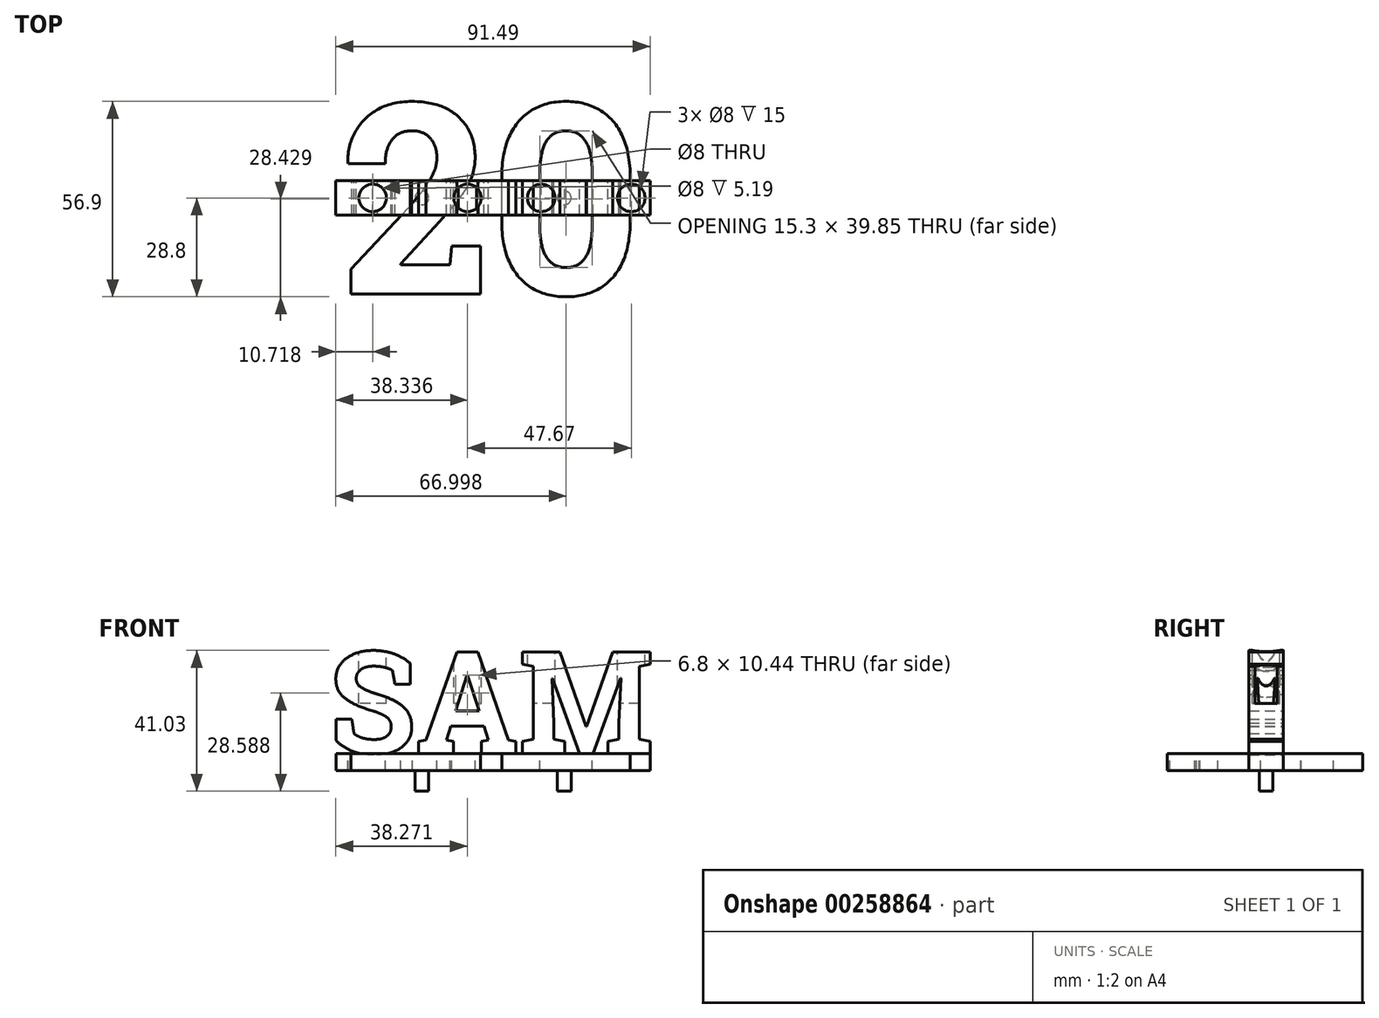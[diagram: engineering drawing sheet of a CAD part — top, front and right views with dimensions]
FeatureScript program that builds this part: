
annotation { "Feature Type Name" : "Feature", "Feature Type Description" : "" }
export const myFeature = defineFeature(function(context is Context, id is Id, definition is map)
    precondition{}
    {
        {
            var Q0;
            Q0=qCreatedBy(makeId("Front.planeOp"),FACE);
            var sketch = newSketch(context, id + "F0", { "sketchPlane" : qUnion([Q0])});
            skText(sketch, "E0", { "text": "SAM", "fontName": "RobotoSlab-Bold.ttf"});
            const initialGuessF0  = {"E0": [-0.048, 0, 1, 0, 0.03]};
            skSetInitialGuess(sketch, initialGuessF0);
            skSolve(sketch);
        }
        {
            var Q0;
            Q0 = qSketchRegion(id + "F0", true);
            extrude(context, id + "F1", {"entities" : qUnion([Q0]), "depth" : 10 * mm});
        }
        {
            var Q0;
            Q0=makeQuery(id+"F1.opExtrude","SWEPT_FACE",FACE,{"disambiguationData":[OSD([sQuery(id+"F0.wireOp",EDGE,"E0.sketch_text.stroke-44")])]});
            var sketch = newSketch(context, id + "F2", { "sketchPlane" : qUnion([Q0])});
            skLineSegment(sketch, "E1.bottom", {"start": v(45.46, 10) * mm, "end": v(-45.97, 10) * mm});
            skLineSegment(sketch, "E1.top", {"start": v(45.46, 0) * mm, "end": v(-45.97, 0) * mm});
            skLineSegment(sketch, "E1.left", {"start": v(45.46, 10) * mm, "end": v(45.46, 0) * mm});
            skLineSegment(sketch, "E1.right", {"start": v(-45.97, 10) * mm, "end": v(-45.97, 0) * mm});
            skSolve(sketch);
        }
        {
            var Q0;
            Q0 = qSketchRegion(id + "F2", true);
            extrude(context, id + "F3", {"entities" : qUnion([Q0]), "depth" : 5 * mm});
        }
        {
            var Q0;
            Q0=makeQuery(id+"F3.opExtrude","CAP_FACE",FACE,{"disambiguationData":[OSD([sQuery(id+"F2.wireOp",EDGE,"E1.bottom"),sQuery(id+"F2.wireOp",EDGE,"E1.top"),sQuery(id+"F2.wireOp",EDGE,"E1.left"),sQuery(id+"F2.wireOp",EDGE,"E1.right")])],"isStart":true});
            var sketch = newSketch(context, id + "F4", { "sketchPlane" : qUnion([Q0])});
            skText(sketch, "E2", { "text": "20", "fontName": "RobotoSlab-Bold.ttf"});
            const initialGuessF4  = {"E2": [-0.04442, -0.033, 1, 0, 0.056]};
            skSetInitialGuess(sketch, initialGuessF4);
            skSolve(sketch);
        }
        {
            var Q0;
            Q0 = qSketchRegion(id + "F4", true);
            extrude(context, id + "F5", {"entities" : qUnion([Q0]), "oppositeDirection" : true, "depth" : 5 * mm});
        }
        {
            var Q0;
            Q0=makeQuery(id+"F1.opExtrude","SWEPT_FACE",FACE,{"disambiguationData":[OSD([sQuery(id+"F0.wireOp",EDGE,"E0.sketch_text.stroke-70")])]});
            var sketch = newSketch(context, id + "F6", { "sketchPlane" : qUnion([Q0])});
            skCircle(sketch, "E3", {"center": v(39.98, -5) * mm, "radius": 4 * mm});
            skPoint(sketch, "E3.centerSnap0", {"position": v(39.98, 0) * mm});
            skCircle(sketch, "E4", {"center": v(-35.31, -5) * mm, "radius": 4 * mm});
            skCircle(sketch, "E5", {"center": v(13.75, -5) * mm, "radius": 4 * mm});
            skCircle(sketch, "E6", {"center": v(-7.7, -5) * mm, "radius": 4 * mm});
            skSolve(sketch);
        }
        {
            var Q0;
            Q0 = qSketchRegion(id + "F6", true);
            extrude(context, id + "F7", {"entities" : qUnion([Q0]), "operationType" : NewBodyOperationType.REMOVE, "oppositeDirection" : true, "depth" : 15 * mm, "hasSecondDirection" : true, "secondDirectionOppositeDirection" : false, "secondDirectionDepth" : 25 * mm});
        }
        {
            var Q0;
            Q0=makeQuery(id+"F3.opExtrude","CAP_FACE",FACE,{"disambiguationData":[OSD([sQuery(id+"F2.wireOp",EDGE,"E1.bottom"),sQuery(id+"F2.wireOp",EDGE,"E1.top"),sQuery(id+"F2.wireOp",EDGE,"E1.left"),sQuery(id+"F2.wireOp",EDGE,"E1.right")])],"isStart":false});
            var sketch = newSketch(context, id + "F8", { "sketchPlane" : qUnion([Q0])});
            skCircle(sketch, "E7", {"center": v(-20.97, 5) * mm, "radius": 2 * mm});
            skCircle(sketch, "E8", {"center": v(20.46, 5) * mm, "radius": 2 * mm});
            skSolve(sketch);
        }
        {
            var Q0;
            Q0 = qSketchRegion(id + "F8", true);
            extrude(context, id + "F9", {"entities" : qUnion([Q0]), "depth" : 6 * mm});
        }
    });
